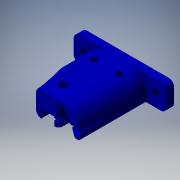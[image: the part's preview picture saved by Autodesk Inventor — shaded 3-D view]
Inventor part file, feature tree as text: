
AUTODESK INVENTOR PART (.ipt)
format: ipt  version: 2016 (Build 200138000, 138)  size: 352,768 bytes
history: native  units: in
note: dims shown in document units (in); Inventor stores cm internally (conversion verified against a paired STEP export)
features: sketch x3, extrude x3, fillet x2, projected_geometry x2, other x1
ambient origin geometry x8: Origin, YZ Plane, XZ Plane, XY Plane, X Axis, Y Axis, Z Axis, Center Point
bodies: Solid1 (feature_tree)
feature tree (11):
  sketch  "Sketch1"  dims[d2=1.122in d3=0.561in d4=0.3937in d5=0.0in]
  extrude  "Extrusion1"  Depth=0.3937in TaperAngle=0.0deg
  extrude  "Extrusion4"  Depth=0.2362in TaperAngle=360.0deg
  fillet  "Fillet3"  Radius=0.2362in
  extrude  "Extrusion2"  Depth=0.1181in TaperAngle=0.0deg
  fillet  "Fillet1"  Radius=0.1575in
  sketch  "Sketch2"  dims[d6=0.1181in d7=2.3622in d9=360.0deg d11=0.2362in]
  projected_geometry  "Projected Loop1"
  sketch  "Sketch3"  dims[d12=0.2362in d13=0.1181in d14=0.0in d15=0.1575in d16=0.0in d17=0.0in d18=0.315in d19=0.315in d23=0.1181in d24=0.1575in d25=0.374in d26=0.187in d27=0.1575in d28=0.187in d29=0.1181in d30=0.0in d31=0.0787in]
  projected_geometry  "Projected Loop3"
  other  "_retractable_-_Imported1_"
